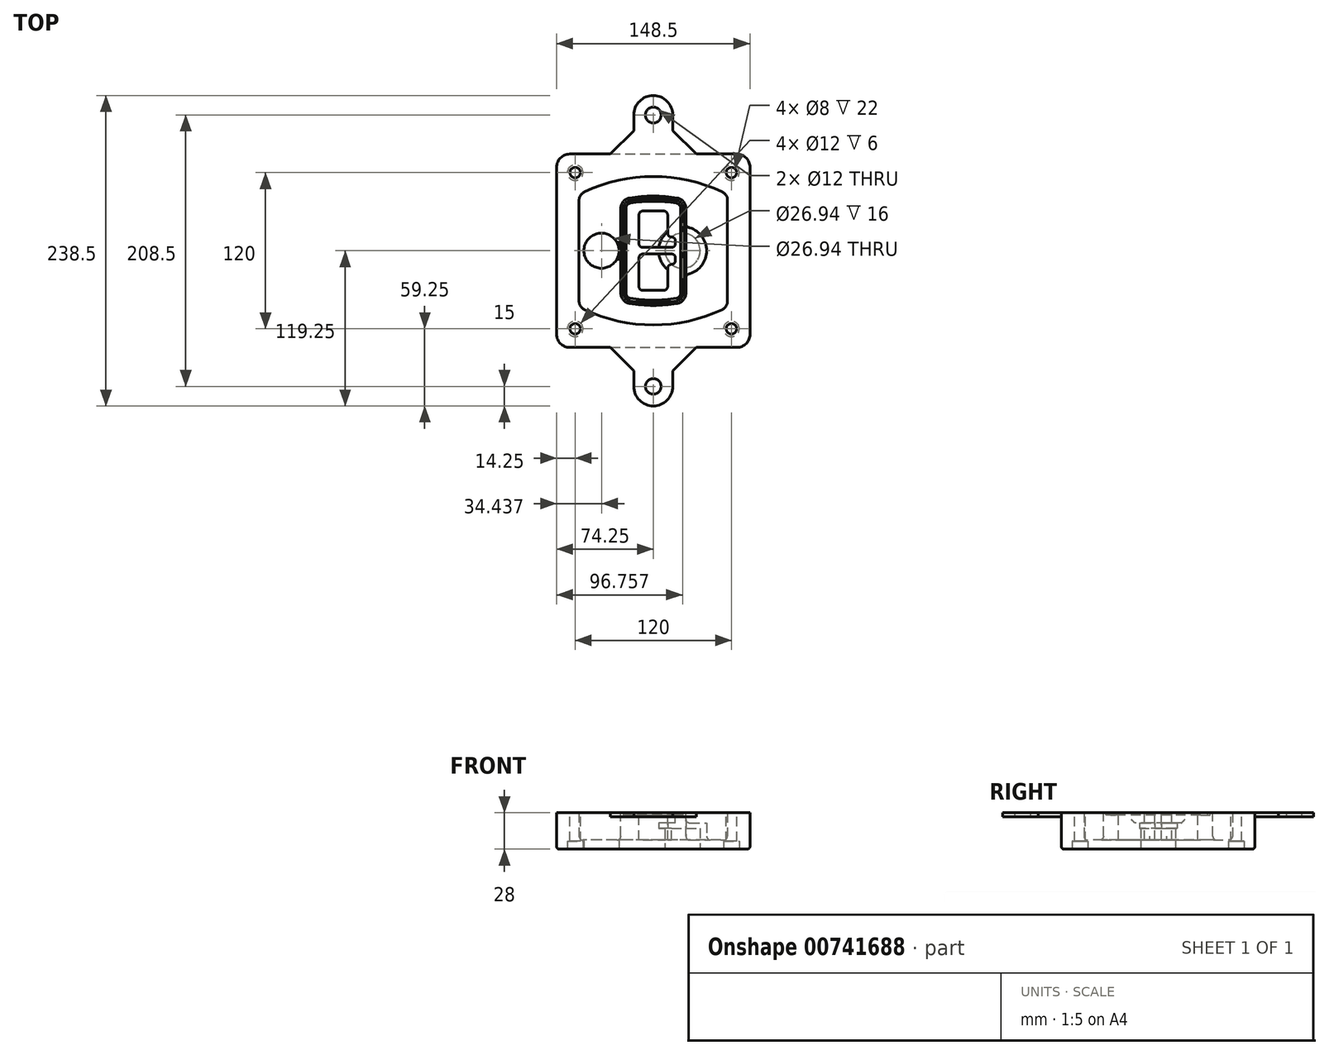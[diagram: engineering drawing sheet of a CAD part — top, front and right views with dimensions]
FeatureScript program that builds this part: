
annotation { "Feature Type Name" : "Feature", "Feature Type Description" : "" }
export const myFeature = defineFeature(function(context is Context, id is Id, definition is map)
    precondition{}
    {
        {
            var Q0;
            Q0=qCreatedBy(makeId("Top.planeOp"),FACE);
            var sketch = newSketch(context, id + "F0", { "sketchPlane" : qUnion([Q0])});
            skPoint(sketch, "E0.rect.middle", {"position": v(0, 0) * mm});
            skLineSegment(sketch, "E1.bottom", {"start": v(-64.25, -74.25) * mm, "end": v(64.25, -74.25) * mm});
            skLineSegment(sketch, "E1.top", {"start": v(-64.25, 74.25) * mm, "end": v(64.25, 74.25) * mm});
            skLineSegment(sketch, "E1.left", {"start": v(-74.25, -64.25) * mm, "end": v(-74.25, 64.25) * mm});
            skLineSegment(sketch, "E1.right", {"start": v(74.25, -64.25) * mm, "end": v(74.25, 64.25) * mm});
            skLineSegment(sketch, "E2", {"start": v(-74.25, 74.25) * mm, "end": v(74.25, -74.25) * mm, "construction": true});
            skLineSegment(sketch, "E3", {"start": v(74.25, 74.25) * mm, "end": v(-74.25, -74.25) * mm, "construction": true});
            skCircle(sketch, "E4", {"center": v(-60, 60) * mm, "radius": 4 * mm});
            skCircle(sketch, "E5", {"center": v(60, 60) * mm, "radius": 4 * mm});
            skCircle(sketch, "E6", {"center": v(60, -60) * mm, "radius": 4 * mm});
            skCircle(sketch, "E7", {"center": v(-60, -60) * mm, "radius": 4 * mm});
            skLineSegment(sketch, "E8", {"start": v(-60, 60) * mm, "end": v(60, 60) * mm, "construction": true});
            skLineSegment(sketch, "E9", {"start": v(60, 60) * mm, "end": v(60, -60) * mm, "construction": true});
            skLineSegment(sketch, "E10", {"start": v(60, -60) * mm, "end": v(-60, -60) * mm, "construction": true});
            skLineSegment(sketch, "E11", {"start": v(-60, -60) * mm, "end": v(-60, 60) * mm, "construction": true});
            skLineSegment(sketch, "E12", {"start": v(-60, 38.83) * mm, "end": v(-60, -38.83) * mm});
            skLineSegment(sketch, "E13", {"start": v(60, 38.83) * mm, "end": v(60, -38.83) * mm});
            skArc(sketch, "E14", {"start": v(54.26, 47.88) * mm, "mid": v(0, 60) * mm, "end": v(-54.26, 47.88) * mm});
            skArc(sketch, "E15", {"start": v(-54.26, -47.88) * mm, "mid": v(0, -60) * mm, "end": v(54.26, -47.88) * mm});
            skLineSegment(sketch, "E16", {"start": v(-60, 0) * mm, "end": v(60, 0) * mm, "construction": true});
            skPoint(sketch, "E17.visualSharp", {"position": v(-60, -45) * mm});
            skArc(sketch, "E17.filletArc", {"start": v(-60, -38.83) * mm, "mid": v(-58.44, -44.2) * mm, "end": v(-54.26, -47.88) * mm});
            skPoint(sketch, "E18.visualSharp", {"position": v(-60, 45) * mm});
            skArc(sketch, "E18.filletArc", {"start": v(-54.26, 47.88) * mm, "mid": v(-58.44, 44.2) * mm, "end": v(-60, 38.83) * mm});
            skPoint(sketch, "E19.visualSharp", {"position": v(60, 45) * mm});
            skArc(sketch, "E19.filletArc", {"start": v(60, 38.83) * mm, "mid": v(58.44, 44.2) * mm, "end": v(54.26, 47.88) * mm});
            skPoint(sketch, "E20.visualSharp", {"position": v(60, -45) * mm});
            skArc(sketch, "E20.filletArc", {"start": v(54.26, -47.88) * mm, "mid": v(58.44, -44.2) * mm, "end": v(60, -38.83) * mm});
            skPoint(sketch, "E21.visualSharp", {"position": v(-74.25, 74.25) * mm});
            skArc(sketch, "E21.filletArc", {"start": v(-64.25, 74.25) * mm, "mid": v(-71.32, 71.32) * mm, "end": v(-74.25, 64.25) * mm});
            skPoint(sketch, "E22.visualSharp", {"position": v(74.25, 74.25) * mm});
            skArc(sketch, "E22.filletArc", {"start": v(74.25, 64.25) * mm, "mid": v(71.32, 71.32) * mm, "end": v(64.25, 74.25) * mm});
            skPoint(sketch, "E23.visualSharp", {"position": v(74.25, -74.25) * mm});
            skArc(sketch, "E23.filletArc", {"start": v(64.25, -74.25) * mm, "mid": v(71.32, -71.32) * mm, "end": v(74.25, -64.25) * mm});
            skPoint(sketch, "E24.visualSharp", {"position": v(-74.25, -74.25) * mm});
            skArc(sketch, "E24.filletArc", {"start": v(-74.25, -64.25) * mm, "mid": v(-71.32, -71.32) * mm, "end": v(-64.25, -74.25) * mm});
            skArc(sketch, "E25.0", {"start": v(57, 38.83) * mm, "mid": v(55.9, 42.58) * mm, "end": v(52.98, 45.17) * mm});
            skLineSegment(sketch, "E25.1", {"start": v(57, 38.83) * mm, "end": v(57, -38.83) * mm});
            skArc(sketch, "E25.2", {"start": v(52.98, -45.17) * mm, "mid": v(55.9, -42.58) * mm, "end": v(57, -38.83) * mm});
            skArc(sketch, "E25.3", {"start": v(-52.98, -45.17) * mm, "mid": v(0, -57) * mm, "end": v(52.98, -45.17) * mm});
            skArc(sketch, "E25.4", {"start": v(-57, -38.83) * mm, "mid": v(-55.9, -42.58) * mm, "end": v(-52.98, -45.17) * mm});
            skArc(sketch, "E25.5", {"start": v(52.98, 45.17) * mm, "mid": v(0, 57) * mm, "end": v(-52.98, 45.17) * mm});
            skLineSegment(sketch, "E25.6", {"start": v(-57, 38.83) * mm, "end": v(-57, -38.83) * mm});
            skArc(sketch, "E25.7", {"start": v(-52.98, 45.17) * mm, "mid": v(-55.9, 42.58) * mm, "end": v(-57, 38.83) * mm});
            skArc(sketch, "E26.0", {"start": v(-55.96, 51.5) * mm, "mid": v(-61.82, 46.33) * mm, "end": v(-64, 38.83) * mm});
            skArc(sketch, "E26.1", {"start": v(55.96, 51.5) * mm, "mid": v(0, 64) * mm, "end": v(-55.96, 51.5) * mm});
            skArc(sketch, "E26.2", {"start": v(64, 38.83) * mm, "mid": v(61.82, 46.33) * mm, "end": v(55.96, 51.5) * mm});
            skLineSegment(sketch, "E26.3", {"start": v(64, 38.83) * mm, "end": v(64, -38.83) * mm});
            skArc(sketch, "E26.4", {"start": v(55.96, -51.5) * mm, "mid": v(61.82, -46.33) * mm, "end": v(64, -38.83) * mm});
            skLineSegment(sketch, "E26.5", {"start": v(-64, 38.83) * mm, "end": v(-64, -38.83) * mm});
            skArc(sketch, "E26.6", {"start": v(-55.96, -51.5) * mm, "mid": v(0, -64) * mm, "end": v(55.96, -51.5) * mm});
            skArc(sketch, "E26.7", {"start": v(-64, -38.83) * mm, "mid": v(-61.82, -46.33) * mm, "end": v(-55.96, -51.5) * mm});
            skSolve(sketch);
        }
        {
            var Q0;
            Q0=makeQuery(id+"F0.imprint","IMPRINT",FACE,{"disambiguationData":[TD([[makeQuery(id+"F0.imprint","IMPRINT",EDGE,{"derivedFrom":sQuery(id+"F0.wireOp",EDGE,"E1.bottom")}),1.0]])]});
            var Q1;
            Q1=makeQuery(id+"F0.imprint","IMPRINT",FACE,{"disambiguationData":[TD([[makeQuery(id+"F0.imprint","IMPRINT",EDGE,{"derivedFrom":sQuery(id+"F0.wireOp",EDGE,"E12")}),1.0]])]});
            var Q2;
            Q2=makeQuery(id+"F0.imprint","IMPRINT",FACE,{"disambiguationData":[TD([[makeQuery(id+"F0.imprint","IMPRINT",EDGE,{"derivedFrom":sQuery(id+"F0.wireOp",EDGE,"E25.0")}),1.0]])]});
            var Q3;
            Q3=makeQuery(id+"F0.imprint","IMPRINT",FACE,{"disambiguationData":[TD([[makeQuery(id+"F0.imprint","IMPRINT",EDGE,{"derivedFrom":sQuery(id+"F0.wireOp",EDGE,"E12")}),-1.0]])]});
            extrude(context, id + "F1", {"entities" : qUnion([Q0, Q1, Q2, Q3]), "oppositeDirection" : true, "depth" : 25 * mm});
        }
        {
            var Q0;
            Q0=makeQuery(id+"F0.imprint","IMPRINT",FACE,{"disambiguationData":[TD([[makeQuery(id+"F0.imprint","IMPRINT",EDGE,{"derivedFrom":sQuery(id+"F0.wireOp",EDGE,"E12")}),1.0]])]});
            extrude(context, id + "F2", {"entities" : qUnion([Q0]), "operationType" : NewBodyOperationType.ADD, "depth" : 3 * mm});
        }
        {
            var Q0;
            Q0=makeQuery(id+"F0.imprint","IMPRINT",FACE,{"disambiguationData":[TD([[makeQuery(id+"F0.imprint","IMPRINT",EDGE,{"derivedFrom":sQuery(id+"F0.wireOp",EDGE,"E25.0")}),1.0]])]});
            extrude(context, id + "F3", {"entities" : qUnion([Q0]), "operationType" : NewBodyOperationType.REMOVE, "oppositeDirection" : true, "depth" : 18 * mm});
        }
        {
            var Q0;
            Q0=makeQuery(id+"F2.opExtrude","CAP_FACE",FACE,{"disambiguationData":[OSD([sQuery(id+"F0.wireOp",EDGE,"E12"),sQuery(id+"F0.wireOp",EDGE,"E13"),sQuery(id+"F0.wireOp",EDGE,"E14"),sQuery(id+"F0.wireOp",EDGE,"E15"),sQuery(id+"F0.wireOp",EDGE,"E17.filletArc"),sQuery(id+"F0.wireOp",EDGE,"E18.filletArc"),sQuery(id+"F0.wireOp",EDGE,"E19.filletArc"),sQuery(id+"F0.wireOp",EDGE,"E20.filletArc"),sQuery(id+"F0.wireOp",EDGE,"E25.0"),sQuery(id+"F0.wireOp",EDGE,"E25.1"),sQuery(id+"F0.wireOp",EDGE,"E25.2"),sQuery(id+"F0.wireOp",EDGE,"E25.3"),sQuery(id+"F0.wireOp",EDGE,"E25.4"),sQuery(id+"F0.wireOp",EDGE,"E25.5"),sQuery(id+"F0.wireOp",EDGE,"E25.6"),sQuery(id+"F0.wireOp",EDGE,"E25.7")])],"isStart":false});
            var sketch = newSketch(context, id + "F4", { "sketchPlane" : qUnion([Q0])});
            skArc(sketch, "E27.0", {"start": v(-18.34, -40.45) * mm, "mid": v(0, -42) * mm, "end": v(18.34, -40.45) * mm});
            skArc(sketch, "E28.0", {"start": v(18.34, 40.45) * mm, "mid": v(0, 42) * mm, "end": v(-18.34, 40.45) * mm});
            skLineSegment(sketch, "E29", {"start": v(-25, 32.57) * mm, "end": v(-25, -32.57) * mm});
            skLineSegment(sketch, "E30", {"start": v(25, 32.57) * mm, "end": v(25, -32.57) * mm});
            skLineSegment(sketch, "E31", {"start": v(-25, 39.1) * mm, "end": v(25, 39.1) * mm, "construction": true});
            skLineSegment(sketch, "E32", {"start": v(-25, -39.1) * mm, "end": v(25, -39.1) * mm, "construction": true});
            skPoint(sketch, "E33.visualSharp", {"position": v(-25, 39.1) * mm});
            skArc(sketch, "E33.filletArc", {"start": v(-18.34, 40.45) * mm, "mid": v(-23.11, 37.73) * mm, "end": v(-25, 32.57) * mm});
            skPoint(sketch, "E34.visualSharp", {"position": v(25, 39.1) * mm});
            skArc(sketch, "E34.filletArc", {"start": v(25, 32.57) * mm, "mid": v(23.11, 37.73) * mm, "end": v(18.34, 40.45) * mm});
            skPoint(sketch, "E35.visualSharp", {"position": v(25, -39.1) * mm});
            skArc(sketch, "E35.filletArc", {"start": v(18.34, -40.45) * mm, "mid": v(23.11, -37.73) * mm, "end": v(25, -32.57) * mm});
            skPoint(sketch, "E36.visualSharp", {"position": v(-25, -39.1) * mm});
            skArc(sketch, "E36.filletArc", {"start": v(-25, -32.57) * mm, "mid": v(-23.11, -37.73) * mm, "end": v(-18.34, -40.45) * mm});
            skArc(sketch, "E37.0", {"start": v(52.98, 45.17) * mm, "mid": v(0, 57) * mm, "end": v(-52.98, 45.17) * mm});
            skArc(sketch, "E37.1", {"start": v(-52.98, 45.17) * mm, "mid": v(-55.9, 42.58) * mm, "end": v(-57, 38.83) * mm});
            skLineSegment(sketch, "E37.2", {"start": v(-57, 38.83) * mm, "end": v(-57, -38.83) * mm});
            skArc(sketch, "E37.3", {"start": v(-57, -38.83) * mm, "mid": v(-55.9, -42.58) * mm, "end": v(-52.98, -45.17) * mm});
            skArc(sketch, "E37.4", {"start": v(-52.98, -45.17) * mm, "mid": v(0, -57) * mm, "end": v(52.98, -45.17) * mm});
            skArc(sketch, "E37.5", {"start": v(52.98, -45.17) * mm, "mid": v(55.9, -42.58) * mm, "end": v(57, -38.83) * mm});
            skLineSegment(sketch, "E37.6", {"start": v(57, 38.83) * mm, "end": v(57, -38.83) * mm});
            skArc(sketch, "E37.7", {"start": v(57, 38.83) * mm, "mid": v(55.9, 42.58) * mm, "end": v(52.98, 45.17) * mm});
            skLineSegment(sketch, "E38.0", {"start": v(23, 32.57) * mm, "end": v(23, -32.57) * mm});
            skArc(sketch, "E38.1", {"start": v(18, -38.48) * mm, "mid": v(21.58, -36.44) * mm, "end": v(23, -32.57) * mm});
            skArc(sketch, "E38.2", {"start": v(-18, -38.48) * mm, "mid": v(0, -40) * mm, "end": v(18, -38.48) * mm});
            skArc(sketch, "E38.3", {"start": v(-23, -32.57) * mm, "mid": v(-21.58, -36.44) * mm, "end": v(-18, -38.48) * mm});
            skLineSegment(sketch, "E38.4", {"start": v(-23, 32.57) * mm, "end": v(-23, -32.57) * mm});
            skArc(sketch, "E38.5", {"start": v(23, 32.57) * mm, "mid": v(21.58, 36.44) * mm, "end": v(18, 38.48) * mm});
            skArc(sketch, "E38.6", {"start": v(-18, 38.48) * mm, "mid": v(-21.58, 36.44) * mm, "end": v(-23, 32.57) * mm});
            skArc(sketch, "E38.7", {"start": v(18, 38.48) * mm, "mid": v(0, 40) * mm, "end": v(-18, 38.48) * mm});
            skArc(sketch, "E39.0", {"start": v(21, 32.57) * mm, "mid": v(20.06, 35.15) * mm, "end": v(17.67, 36.5) * mm});
            skLineSegment(sketch, "E39.1", {"start": v(21, 32.57) * mm, "end": v(21, -32.57) * mm});
            skArc(sketch, "E39.2", {"start": v(17.67, -36.5) * mm, "mid": v(20.06, -35.15) * mm, "end": v(21, -32.57) * mm});
            skArc(sketch, "E39.3", {"start": v(-17.67, -36.5) * mm, "mid": v(0, -38) * mm, "end": v(17.67, -36.5) * mm});
            skArc(sketch, "E39.4", {"start": v(-21, -32.57) * mm, "mid": v(-20.06, -35.15) * mm, "end": v(-17.67, -36.5) * mm});
            skArc(sketch, "E39.5", {"start": v(17.67, 36.5) * mm, "mid": v(0, 38) * mm, "end": v(-17.67, 36.5) * mm});
            skLineSegment(sketch, "E39.6", {"start": v(-21, 32.57) * mm, "end": v(-21, -32.57) * mm});
            skArc(sketch, "E39.7", {"start": v(-17.67, 36.5) * mm, "mid": v(-20.06, 35.15) * mm, "end": v(-21, 32.57) * mm});
            skLineSegment(sketch, "E40", {"start": v(-25, 0) * mm, "end": v(25, 0) * mm, "construction": true});
            skLineSegment(sketch, "E41", {"start": v(-11, 5.5) * mm, "end": v(-11, 27.5) * mm});
            skLineSegment(sketch, "E42", {"start": v(-8, 30.5) * mm, "end": v(8, 30.5) * mm});
            skLineSegment(sketch, "E43", {"start": v(11, 27.5) * mm, "end": v(11, 13.5) * mm});
            skLineSegment(sketch, "E44", {"start": v(14, 10.5) * mm, "end": v(14, 10.5) * mm});
            skLineSegment(sketch, "E45", {"start": v(17, 7.5) * mm, "end": v(17, 5.5) * mm});
            skLineSegment(sketch, "E46", {"start": v(14, 2.5) * mm, "end": v(-8, 2.5) * mm});
            skPoint(sketch, "E47.visualSharp", {"position": v(-11, 30.5) * mm});
            skArc(sketch, "E47.filletArc", {"start": v(-8, 30.5) * mm, "mid": v(-10.12, 29.62) * mm, "end": v(-11, 27.5) * mm});
            skPoint(sketch, "E48.visualSharp", {"position": v(11, 30.5) * mm});
            skArc(sketch, "E48.filletArc", {"start": v(11, 27.5) * mm, "mid": v(10.12, 29.62) * mm, "end": v(8, 30.5) * mm});
            skPoint(sketch, "E49.visualSharp", {"position": v(11, 10.5) * mm});
            skArc(sketch, "E49.filletArc", {"start": v(11, 13.5) * mm, "mid": v(11.88, 11.38) * mm, "end": v(14, 10.5) * mm});
            skPoint(sketch, "E50.visualSharp", {"position": v(17, 10.5) * mm});
            skArc(sketch, "E50.filletArc", {"start": v(17, 7.5) * mm, "mid": v(16.12, 9.62) * mm, "end": v(14, 10.5) * mm});
            skPoint(sketch, "E51.visualSharp", {"position": v(17, 2.5) * mm});
            skArc(sketch, "E51.filletArc", {"start": v(14, 2.5) * mm, "mid": v(16.12, 3.38) * mm, "end": v(17, 5.5) * mm});
            skPoint(sketch, "E52.visualSharp", {"position": v(-11, 2.5) * mm});
            skArc(sketch, "E52.filletArc", {"start": v(-11, 5.5) * mm, "mid": v(-10.12, 3.38) * mm, "end": v(-8, 2.5) * mm});
            skLineSegment(sketch, "E53.0.MirrorCS", {"start": v(14, -2.5) * mm, "end": v(-8, -2.5) * mm});
            skArc(sketch, "E54.0.MirrorCS", {"start": v(-11, -5.5) * mm, "mid": v(-10.12, -3.38) * mm, "end": v(-8, -2.5) * mm});
            skLineSegment(sketch, "E55.0.MirrorCS", {"start": v(-11, -5.5) * mm, "end": v(-11, -27.5) * mm});
            skArc(sketch, "E56.0.MirrorCS", {"start": v(-8, -30.5) * mm, "mid": v(-10.12, -29.62) * mm, "end": v(-11, -27.5) * mm});
            skLineSegment(sketch, "E57.0.MirrorCS", {"start": v(-8, -30.5) * mm, "end": v(8, -30.5) * mm});
            skArc(sketch, "E58.0.MirrorCS", {"start": v(11, -27.5) * mm, "mid": v(10.12, -29.62) * mm, "end": v(8, -30.5) * mm});
            skLineSegment(sketch, "E59.0.MirrorCS", {"start": v(11, -27.5) * mm, "end": v(11, -13.5) * mm});
            skArc(sketch, "E60.0.MirrorCS", {"start": v(11, -13.5) * mm, "mid": v(11.88, -11.38) * mm, "end": v(14, -10.5) * mm});
            skArc(sketch, "E61.0.MirrorCS", {"start": v(17, -7.5) * mm, "mid": v(16.12, -9.62) * mm, "end": v(14, -10.5) * mm});
            skLineSegment(sketch, "E62.0.MirrorCS", {"start": v(17, -7.5) * mm, "end": v(17, -5.5) * mm});
            skArc(sketch, "E63.0.MirrorCS", {"start": v(14, -2.5) * mm, "mid": v(16.12, -3.38) * mm, "end": v(17, -5.5) * mm});
            skSolve(sketch);
        }
        {
            var Q0;
            Q0=makeQuery(id+"F4.imprint","IMPRINT",FACE,{"disambiguationData":[TD([[makeQuery(id+"F4.imprint","IMPRINT",EDGE,{"derivedFrom":sQuery(id+"F4.wireOp",EDGE,"E27.0")}),1.0]])]});
            var Q1;
            Q1=makeQuery(id+"F4.imprint","IMPRINT",FACE,{"disambiguationData":[TD([[makeQuery(id+"F4.imprint","IMPRINT",EDGE,{"derivedFrom":sQuery(id+"F4.wireOp",EDGE,"E38.0")}),-1.0]])]});
            var Q2;
            Q2=makeQuery(id+"F4.imprint","IMPRINT",FACE,{"disambiguationData":[TD([[makeQuery(id+"F4.imprint","IMPRINT",EDGE,{"derivedFrom":sQuery(id+"F4.wireOp",EDGE,"E39.0")}),1.0]])]});
            extrude(context, id + "F5", {"entities" : qUnion([Q0, Q1, Q2]), "operationType" : NewBodyOperationType.ADD, "endBound" : BoundingType.UP_TO_NEXT, "oppositeDirection" : true, "depth" : 25 * mm});
        }
        {
            var Q0;
            Q0=makeQuery(id+"F4.imprint","IMPRINT",FACE,{"disambiguationData":[TD([[makeQuery(id+"F4.imprint","IMPRINT",EDGE,{"derivedFrom":sQuery(id+"F4.wireOp",EDGE,"E38.0")}),-1.0]])]});
            extrude(context, id + "F6", {"entities" : qUnion([Q0]), "operationType" : NewBodyOperationType.REMOVE, "oppositeDirection" : true, "depth" : 2 * mm});
        }
        {
            var Q0;
            Q0=makeQuery(id+"F1.opExtrude","CAP_FACE",FACE,{"disambiguationData":[OSD([sQuery(id+"F0.wireOp",EDGE,"E1.bottom"),sQuery(id+"F0.wireOp",EDGE,"E1.top"),sQuery(id+"F0.wireOp",EDGE,"E1.left"),sQuery(id+"F0.wireOp",EDGE,"E1.right"),sQuery(id+"F0.wireOp",EDGE,"E4"),sQuery(id+"F0.wireOp",EDGE,"E5"),sQuery(id+"F0.wireOp",EDGE,"E6"),sQuery(id+"F0.wireOp",EDGE,"E7"),sQuery(id+"F0.wireOp",EDGE,"E21.filletArc"),sQuery(id+"F0.wireOp",EDGE,"E22.filletArc"),sQuery(id+"F0.wireOp",EDGE,"E23.filletArc"),sQuery(id+"F0.wireOp",EDGE,"E24.filletArc")])],"isStart":false});
            var sketch = newSketch(context, id + "F7", { "sketchPlane" : qUnion([Q0])});
            skCircle(sketch, "E64", {"center": v(22.5, 0) * mm, "radius": 13.47 * mm});
            skCircle(sketch, "E65", {"center": v(-39.81, 0) * mm, "radius": 13.47 * mm});
            skLineSegment(sketch, "E66", {"start": v(74.25, 0) * mm, "end": v(-74.25, 0) * mm});
            skCircle(sketch, "E67", {"center": v(22.5, 0) * mm, "radius": 18.47 * mm});
            skCircle(sketch, "E68", {"center": v(60, -60) * mm, "radius": 6 * mm});
            skCircle(sketch, "E69", {"center": v(-60, -60) * mm, "radius": 6 * mm});
            skCircle(sketch, "E70", {"center": v(-60, 60) * mm, "radius": 6 * mm});
            skCircle(sketch, "E71", {"center": v(60, 60) * mm, "radius": 6 * mm});
            skSolve(sketch);
        }
        {
            var Q0;
            {var subQ1=sQuery(id+"F7.wireOp",EDGE,"E66");var subQ4=sQuery(id+"F7.wireOp",EDGE,"E64");var subQ6=makeQuery(id+"F7.imprint","INTERSECT",VERTEX,{"disambiguationData":[OD(0.0)],"derivedFrom":[subQ4,subQ1]});Q0=makeQuery(id+"F7.imprint","IMPRINT",FACE,{"disambiguationData":[TD([[makeQuery(id+"F7.imprint","IMPRINT",EDGE,{"disambiguationData":[TD([[subQ6,-1.0]])],"derivedFrom":subQ4}),-1.0]])]});}
            var Q1;
            {var subQ0=sQuery(id+"F7.wireOp",EDGE,"E66");var subQ1=sQuery(id+"F7.wireOp",EDGE,"E64");var subQ3=makeQuery(id+"F7.imprint","INTERSECT",VERTEX,{"disambiguationData":[OD(0.0)],"derivedFrom":[subQ1,subQ0]});Q1=makeQuery(id+"F7.imprint","IMPRINT",FACE,{"disambiguationData":[TD([[makeQuery(id+"F7.imprint","IMPRINT",EDGE,{"disambiguationData":[TD([[subQ3,-1.0]])],"derivedFrom":subQ1}),1.0]])]});}
            var Q2;
            {var subQ0=sQuery(id+"F7.wireOp",EDGE,"E66");var subQ1=sQuery(id+"F7.wireOp",EDGE,"E64");var subQ3=makeQuery(id+"F7.imprint","INTERSECT",VERTEX,{"disambiguationData":[OD(0.0)],"derivedFrom":[subQ1,subQ0]});Q2=makeQuery(id+"F7.imprint","IMPRINT",FACE,{"disambiguationData":[TD([[makeQuery(id+"F7.imprint","IMPRINT",EDGE,{"disambiguationData":[TD([[subQ3,1.0]])],"derivedFrom":subQ1}),1.0]])]});}
            var Q3;
            {var subQ1=sQuery(id+"F7.wireOp",EDGE,"E66");var subQ4=sQuery(id+"F7.wireOp",EDGE,"E64");var subQ6=makeQuery(id+"F7.imprint","INTERSECT",VERTEX,{"disambiguationData":[OD(0.0)],"derivedFrom":[subQ4,subQ1]});Q3=makeQuery(id+"F7.imprint","IMPRINT",FACE,{"disambiguationData":[TD([[makeQuery(id+"F7.imprint","IMPRINT",EDGE,{"disambiguationData":[TD([[subQ6,1.0]])],"derivedFrom":subQ4}),-1.0]])]});}
            extrude(context, id + "F8", {"entities" : qUnion([Q0, Q1, Q2, Q3]), "operationType" : NewBodyOperationType.ADD, "oppositeDirection" : true, "depth" : 20 * mm});
        }
        {
            var Q0;
            {var subQ0=sQuery(id+"F7.wireOp",EDGE,"E66");var subQ1=sQuery(id+"F7.wireOp",EDGE,"E64");var subQ3=makeQuery(id+"F7.imprint","INTERSECT",VERTEX,{"disambiguationData":[OD(0.0)],"derivedFrom":[subQ1,subQ0]});Q0=makeQuery(id+"F7.imprint","IMPRINT",FACE,{"disambiguationData":[TD([[makeQuery(id+"F7.imprint","IMPRINT",EDGE,{"disambiguationData":[TD([[subQ3,-1.0]])],"derivedFrom":subQ1}),1.0]])]});}
            var Q1;
            {var subQ0=sQuery(id+"F7.wireOp",EDGE,"E66");var subQ1=sQuery(id+"F7.wireOp",EDGE,"E64");var subQ3=makeQuery(id+"F7.imprint","INTERSECT",VERTEX,{"disambiguationData":[OD(0.0)],"derivedFrom":[subQ1,subQ0]});Q1=makeQuery(id+"F7.imprint","IMPRINT",FACE,{"disambiguationData":[TD([[makeQuery(id+"F7.imprint","IMPRINT",EDGE,{"disambiguationData":[TD([[subQ3,1.0]])],"derivedFrom":subQ1}),1.0]])]});}
            extrude(context, id + "F9", {"entities" : qUnion([Q0, Q1]), "operationType" : NewBodyOperationType.REMOVE, "oppositeDirection" : true, "depth" : 16 * mm});
        }
        {
            var Q0;
            {var subQ0=sQuery(id+"F7.wireOp",EDGE,"E66");var subQ1=sQuery(id+"F7.wireOp",EDGE,"E65");var subQ3=makeQuery(id+"F7.imprint","INTERSECT",VERTEX,{"disambiguationData":[OD(0.0)],"derivedFrom":[subQ1,subQ0]});Q0=makeQuery(id+"F7.imprint","IMPRINT",FACE,{"disambiguationData":[TD([[makeQuery(id+"F7.imprint","IMPRINT",EDGE,{"disambiguationData":[TD([[subQ3,-1.0]])],"derivedFrom":subQ1}),1.0]])]});}
            var Q1;
            {var subQ0=sQuery(id+"F7.wireOp",EDGE,"E66");var subQ1=sQuery(id+"F7.wireOp",EDGE,"E65");var subQ3=makeQuery(id+"F7.imprint","INTERSECT",VERTEX,{"disambiguationData":[OD(0.0)],"derivedFrom":[subQ1,subQ0]});Q1=makeQuery(id+"F7.imprint","IMPRINT",FACE,{"disambiguationData":[TD([[makeQuery(id+"F7.imprint","IMPRINT",EDGE,{"disambiguationData":[TD([[subQ3,1.0]])],"derivedFrom":subQ1}),1.0]])]});}
            extrude(context, id + "F10", {"entities" : qUnion([Q0, Q1]), "operationType" : NewBodyOperationType.REMOVE, "oppositeDirection" : true, "depth" : 25 * mm});
        }
        {
            var Q0;
            Q0=makeQuery(id+"F7.imprint","IMPRINT",FACE,{"disambiguationData":[TD([[makeQuery(id+"F7.imprint","IMPRINT",EDGE,{"derivedFrom":sQuery(id+"F7.wireOp",EDGE,"E68")}),1.0]])]});
            var Q1;
            Q1=makeQuery(id+"F7.imprint","IMPRINT",FACE,{"disambiguationData":[TD([[makeQuery(id+"F7.imprint","IMPRINT",EDGE,{"derivedFrom":makeQuery(id+"F1.opExtrude","CAP_EDGE",EDGE,{"disambiguationData":[OSD([sQuery(id+"F0.wireOp",EDGE,"E5")])],"isStart":false})}),-1.0]])]});
            var Q2;
            Q2=makeQuery(id+"F7.imprint","IMPRINT",FACE,{"disambiguationData":[TD([[makeQuery(id+"F7.imprint","IMPRINT",EDGE,{"derivedFrom":sQuery(id+"F7.wireOp",EDGE,"E69")}),1.0]])]});
            var Q3;
            Q3=makeQuery(id+"F7.imprint","IMPRINT",FACE,{"disambiguationData":[TD([[makeQuery(id+"F7.imprint","IMPRINT",EDGE,{"derivedFrom":makeQuery(id+"F1.opExtrude","CAP_EDGE",EDGE,{"disambiguationData":[OSD([sQuery(id+"F0.wireOp",EDGE,"E4")])],"isStart":false})}),-1.0]])]});
            var Q4;
            Q4=makeQuery(id+"F7.imprint","IMPRINT",FACE,{"disambiguationData":[TD([[makeQuery(id+"F7.imprint","IMPRINT",EDGE,{"derivedFrom":sQuery(id+"F7.wireOp",EDGE,"E70")}),1.0]])]});
            var Q5;
            Q5=makeQuery(id+"F7.imprint","IMPRINT",FACE,{"disambiguationData":[TD([[makeQuery(id+"F7.imprint","IMPRINT",EDGE,{"derivedFrom":makeQuery(id+"F1.opExtrude","CAP_EDGE",EDGE,{"disambiguationData":[OSD([sQuery(id+"F0.wireOp",EDGE,"E7")])],"isStart":false})}),-1.0]])]});
            var Q6;
            Q6=makeQuery(id+"F7.imprint","IMPRINT",FACE,{"disambiguationData":[TD([[makeQuery(id+"F7.imprint","IMPRINT",EDGE,{"derivedFrom":sQuery(id+"F7.wireOp",EDGE,"E71")}),1.0]])]});
            var Q7;
            Q7=makeQuery(id+"F7.imprint","IMPRINT",FACE,{"disambiguationData":[TD([[makeQuery(id+"F7.imprint","IMPRINT",EDGE,{"derivedFrom":makeQuery(id+"F1.opExtrude","CAP_EDGE",EDGE,{"disambiguationData":[OSD([sQuery(id+"F0.wireOp",EDGE,"E6")])],"isStart":false})}),-1.0]])]});
            extrude(context, id + "F11", {"entities" : qUnion([Q0, Q1, Q2, Q3, Q4, Q5, Q6, Q7]), "operationType" : NewBodyOperationType.REMOVE, "oppositeDirection" : true, "depth" : 6 * mm});
        }
        {
            var Q0;
            Q0=makeQuery(id+"F9.boolean.opBoolean","COPY",FACE,{"derivedFrom":makeQuery(id+"F9.opExtrude","CAP_FACE",FACE,{"disambiguationData":[OSD([sQuery(id+"F7.wireOp",EDGE,"E64")])],"isStart":false})});
            var sketch = newSketch(context, id + "F12", { "sketchPlane" : qUnion([Q0])});
            skArc(sketch, "E72.0", {"start": v(11, 14.45) * mm, "mid": v(6.45, 9.13) * mm, "end": v(4.2, 2.5) * mm});
            skArc(sketch, "E72.1", {"start": v(4.2, -2.5) * mm, "mid": v(6.45, -9.13) * mm, "end": v(11, -14.45) * mm});
            skLineSegment(sketch, "E73", {"start": v(4.2, -2.5) * mm, "end": v(14, -2.5) * mm});
            skLineSegment(sketch, "E74.0", {"start": v(14, 2.5) * mm, "end": v(4.2, 2.5) * mm});
            skArc(sketch, "E74.1", {"start": v(14, 2.5) * mm, "mid": v(16.12, 3.38) * mm, "end": v(17, 5.5) * mm});
            skLineSegment(sketch, "E74.2", {"start": v(17, 7.5) * mm, "end": v(17, 5.5) * mm});
            skArc(sketch, "E74.3", {"start": v(17, 7.5) * mm, "mid": v(16.12, 9.62) * mm, "end": v(14, 10.5) * mm});
            skArc(sketch, "E74.4", {"start": v(11, 13.5) * mm, "mid": v(11.88, 11.38) * mm, "end": v(14, 10.5) * mm});
            skLineSegment(sketch, "E74.5", {"start": v(11, 14.45) * mm, "end": v(11, 13.5) * mm});
            skLineSegment(sketch, "E74.7", {"start": v(14, -2.5) * mm, "end": v(4.2, -2.5) * mm});
            skArc(sketch, "E74.8", {"start": v(14, -2.5) * mm, "mid": v(16.12, -3.38) * mm, "end": v(17, -5.5) * mm});
            skLineSegment(sketch, "E74.9", {"start": v(17, -7.5) * mm, "end": v(17, -5.5) * mm});
            skArc(sketch, "E74.10", {"start": v(17, -7.5) * mm, "mid": v(16.12, -9.62) * mm, "end": v(14, -10.5) * mm});
            skArc(sketch, "E74.11", {"start": v(11, -13.5) * mm, "mid": v(11.88, -11.38) * mm, "end": v(14, -10.5) * mm});
            skLineSegment(sketch, "E74.12", {"start": v(11, -14.45) * mm, "end": v(11, -13.5) * mm});
            skPoint(sketch, "E75.orphan", {"position": v(11, -27.5) * mm});
            skPoint(sketch, "E76.orphan", {"position": v(-8, -2.5) * mm});
            skPoint(sketch, "E77.orphan", {"position": v(-8, 2.5) * mm});
            skPoint(sketch, "E78.orphan", {"position": v(11, 27.5) * mm});
            skSolve(sketch);
        }
        {
            var Q0;
            {var subQ7=sQuery(id+"F12.wireOp",EDGE,"E72.0");var subQ14=sQuery(id+"F12.wireOp",EDGE,"E72.1");var subQ16=sQuery(id+"F12.wireOp",EDGE,"E74.1");var subQ18=sQuery(id+"F12.wireOp",EDGE,"E74.8");Q0=qUnion([makeQuery(id+"F12.imprint","IMPRINT",FACE,{"disambiguationData":[TD([[makeQuery(id+"F12.imprint","IMPRINT",EDGE,{"derivedFrom":subQ7}),1.0]])]}),makeQuery(id+"F12.imprint","IMPRINT",FACE,{"disambiguationData":[TD([[makeQuery(id+"F12.imprint","IMPRINT",EDGE,{"derivedFrom":subQ14}),1.0]])]}),makeQuery(id+"F12.imprint","IMPRINT",FACE,{"disambiguationData":[TD([[makeQuery(id+"F12.imprint","IMPRINT",EDGE,{"derivedFrom":subQ16}),1.0]])]}),makeQuery(id+"F12.imprint","IMPRINT",FACE,{"disambiguationData":[TD([[makeQuery(id+"F12.imprint","IMPRINT",EDGE,{"derivedFrom":subQ18}),-1.0]])]})]);}
            var Q1;
            Q1=makeQuery(id+"F5.boolean.opBoolean","SPLIT",FACE,{"disambiguationData":[TD([makeQuery(id+"F5.opExtrude","SWEPT_FACE",FACE,{"disambiguationData":[OSD([sQuery(id+"F4.wireOp",EDGE,"E41")])]})])],"derivedFrom":makeQuery(id+"F3.boolean.opBoolean","COPY",FACE,{"derivedFrom":makeQuery(id+"F3.opExtrude","CAP_FACE",FACE,{"disambiguationData":[OSD([sQuery(id+"F0.wireOp",EDGE,"E25.0"),sQuery(id+"F0.wireOp",EDGE,"E25.1"),sQuery(id+"F0.wireOp",EDGE,"E25.2"),sQuery(id+"F0.wireOp",EDGE,"E25.3"),sQuery(id+"F0.wireOp",EDGE,"E25.4"),sQuery(id+"F0.wireOp",EDGE,"E25.5"),sQuery(id+"F0.wireOp",EDGE,"E25.6"),sQuery(id+"F0.wireOp",EDGE,"E25.7")])],"isStart":false})})});
            extrude(context, id + "F13", {"entities" : qUnion([Q0]), "operationType" : NewBodyOperationType.REMOVE, "endBound" : BoundingType.UP_TO_SURFACE, "endBoundEntityFace" : qUnion([Q1]), "depth" : 25 * mm});
        }
        {
            var Q0;
            Q0=makeQuery(id+"F3.boolean.opBoolean","COPY",EDGE,{"derivedFrom":makeQuery(id+"F3.opExtrude","CAP_EDGE",EDGE,{"disambiguationData":[OSD([sQuery(id+"F0.wireOp",EDGE,"E25.6")])],"isStart":false})});
            var Q1;
            Q1=makeQuery(id+"F8.boolean.opBoolean","INTERSECT",EDGE,{"derivedFrom":[makeQuery(id+"F5.opExtrude","SWEPT_FACE",FACE,{"disambiguationData":[OSD([sQuery(id+"F4.wireOp",EDGE,"E30")])]}),makeQuery(id+"F8.opExtrude","CAP_FACE",FACE,{"disambiguationData":[OSD([sQuery(id+"F7.wireOp",EDGE,"E67")])],"isStart":false})]});
            var Q2;
            Q2=makeQuery(id+"F8.boolean.opBoolean","INTERSECT",EDGE,{"disambiguationData":[OD(1.0)],"derivedFrom":[makeQuery(id+"F5.opExtrude","SWEPT_FACE",FACE,{"disambiguationData":[OSD([sQuery(id+"F4.wireOp",EDGE,"E30")])]}),makeQuery(id+"F8.opExtrude","SWEPT_FACE",FACE,{"disambiguationData":[OSD([sQuery(id+"F7.wireOp",EDGE,"E67")])]})]});
            var Q3;
            {var subQ0=sQuery(id+"F4.wireOp",EDGE,"E30");Q3=makeQuery(id+"F8.boolean.opBoolean","SPLIT",EDGE,{"disambiguationData":[TD([makeQuery(id+"F5.opExtrude","SWEPT_FACE",FACE,{"disambiguationData":[OSD([sQuery(id+"F4.wireOp",EDGE,"E35.filletArc")])]})])],"derivedFrom":makeQuery(id+"F5.opExtrude","CAP_EDGE",EDGE,{"disambiguationData":[OSD([subQ0])],"isStart":false})});}
            var Q4;
            {var subQ0=sQuery(id+"F0.wireOp",EDGE,"E25.7");var subQ1=sQuery(id+"F0.wireOp",EDGE,"E25.1");var subQ2=sQuery(id+"F0.wireOp",EDGE,"E25.6");var subQ3=sQuery(id+"F0.wireOp",EDGE,"E25.5");var subQ4=sQuery(id+"F0.wireOp",EDGE,"E25.4");var subQ5=sQuery(id+"F0.wireOp",EDGE,"E25.0");var subQ6=sQuery(id+"F0.wireOp",EDGE,"E25.2");var subQ7=sQuery(id+"F0.wireOp",EDGE,"E25.3");Q4=makeQuery(id+"F8.boolean.opBoolean","INTERSECT",EDGE,{"derivedFrom":[makeQuery(id+"F5.boolean.opBoolean","SPLIT",FACE,{"disambiguationData":[TD([makeQuery(id+"F2.opExtrude","SWEPT_FACE",FACE,{"disambiguationData":[OSD([subQ5])]})])],"derivedFrom":makeQuery(id+"F3.boolean.opBoolean","COPY",FACE,{"derivedFrom":makeQuery(id+"F3.opExtrude","CAP_FACE",FACE,{"disambiguationData":[OSD([subQ5,subQ1,subQ6,subQ7,subQ4,subQ3,subQ2,subQ0])],"isStart":false})})}),makeQuery(id+"F8.opExtrude","SWEPT_FACE",FACE,{"disambiguationData":[OSD([sQuery(id+"F7.wireOp",EDGE,"E67")])]})]});}
            var Q5;
            Q5=makeQuery(id+"F8.boolean.opBoolean","INTERSECT",EDGE,{"disambiguationData":[OD(0.0)],"derivedFrom":[makeQuery(id+"F5.opExtrude","SWEPT_FACE",FACE,{"disambiguationData":[OSD([sQuery(id+"F4.wireOp",EDGE,"E30")])]}),makeQuery(id+"F8.opExtrude","SWEPT_FACE",FACE,{"disambiguationData":[OSD([sQuery(id+"F7.wireOp",EDGE,"E67")])]})]});
            fillet(context, id + "F14", {"entities" : qUnion([Q0, Q1, Q2, Q3, Q4, Q5]), "radius" : 3 * mm, "tangentPropagation" : true, "allowEdgeOverflow" : false});
        }
        {
            var Q0;
            Q0=makeQuery(id+"F1.opExtrude","CAP_EDGE",EDGE,{"disambiguationData":[OSD([sQuery(id+"F0.wireOp",EDGE,"E1.bottom")])],"isStart":false});
            fillet(context, id + "F15", {"entities" : qUnion([Q0]), "radius" : 2 * mm, "tangentPropagation" : true, "allowEdgeOverflow" : false});
        }
        {
            var Q0;
            {var subQ0=sQuery(id+"F0.wireOp",EDGE,"E21.filletArc");var subQ1=sQuery(id+"F0.wireOp",EDGE,"E7");var subQ2=sQuery(id+"F0.wireOp",EDGE,"E6");var subQ3=sQuery(id+"F0.wireOp",EDGE,"E5");var subQ4=sQuery(id+"F0.wireOp",EDGE,"E4");var subQ5=sQuery(id+"F0.wireOp",EDGE,"E22.filletArc");var subQ6=sQuery(id+"F0.wireOp",EDGE,"E1.bottom");var subQ7=sQuery(id+"F0.wireOp",EDGE,"E1.right");var subQ8=sQuery(id+"F0.wireOp",EDGE,"E1.top");var subQ9=sQuery(id+"F0.wireOp",EDGE,"E1.left");var subQ10=sQuery(id+"F0.wireOp",EDGE,"E23.filletArc");var subQ11=sQuery(id+"F0.wireOp",EDGE,"E24.filletArc");Q0=makeQuery(id+"F2.boolean.opBoolean","SPLIT",FACE,{"disambiguationData":[TD([makeQuery(id+"F1.opExtrude","SWEPT_FACE",FACE,{"disambiguationData":[OSD([subQ6])]})])],"derivedFrom":makeQuery(id+"F1.opExtrude","CAP_FACE",FACE,{"disambiguationData":[OSD([subQ6,subQ8,subQ9,subQ7,subQ4,subQ3,subQ2,subQ1,subQ0,subQ5,subQ10,subQ11])],"isStart":true})});}
            var sketch = newSketch(context, id + "F16", { "sketchPlane" : qUnion([Q0])});
            skLineSegment(sketch, "E79", {"start": v(0, 74.25) * mm, "end": v(0, 104.25) * mm, "construction": true});
            skCircle(sketch, "E80", {"center": v(0, 104.25) * mm, "radius": 6 * mm});
            skLineSegment(sketch, "E81", {"start": v(-33, 74.25) * mm, "end": v(-15, 92.25) * mm});
            skLineSegment(sketch, "E82", {"start": v(-15, 92.25) * mm, "end": v(-15, 104.25) * mm});
            skLineSegment(sketch, "E83.MirrorCS", {"start": v(15, 92.25) * mm, "end": v(15, 104.25) * mm});
            skLineSegment(sketch, "E84.MirrorCS", {"start": v(33, 74.25) * mm, "end": v(15, 92.25) * mm});
            skArc(sketch, "E85", {"start": v(15, 104.25) * mm, "mid": v(0, 119.25) * mm, "end": v(-15, 104.25) * mm});
            skLineSegment(sketch, "E86", {"start": v(-74.25, 0) * mm, "end": v(74.25, 0) * mm, "construction": true});
            skLineSegment(sketch, "E87.MirrorCS", {"start": v(15, -92.25) * mm, "end": v(15, -104.25) * mm});
            skLineSegment(sketch, "E88.MirrorCS", {"start": v(33, -74.25) * mm, "end": v(15, -92.25) * mm});
            skCircle(sketch, "E89.MirrorC", {"center": v(0, -104.25) * mm, "radius": 6 * mm});
            skLineSegment(sketch, "E90.MirrorCS", {"start": v(0, -74.25) * mm, "end": v(0, -104.25) * mm, "construction": true});
            skLineSegment(sketch, "E91.MirrorCS", {"start": v(-15, -92.25) * mm, "end": v(-15, -104.25) * mm});
            skArc(sketch, "E92.MirrorCS", {"start": v(15, -104.25) * mm, "mid": v(0, -119.25) * mm, "end": v(-15, -104.25) * mm});
            skLineSegment(sketch, "E93.MirrorCS", {"start": v(-33, -74.25) * mm, "end": v(-15, -92.25) * mm});
            skSolve(sketch);
        }
        {
            var Q0;
            Q0=makeQuery(id+"F16.imprint","IMPRINT",FACE,{"disambiguationData":[TD([[makeQuery(id+"F16.imprint","IMPRINT",EDGE,{"derivedFrom":sQuery(id+"F16.wireOp",EDGE,"E80")}),-1.0]])]});
            var Q1;
            Q1=makeQuery(id+"F16.imprint","IMPRINT",FACE,{"disambiguationData":[TD([[makeQuery(id+"F16.imprint","IMPRINT",EDGE,{"derivedFrom":sQuery(id+"F16.wireOp",EDGE,"E87.MirrorCS")}),-1.0]])]});
            var Q2;
            Q2=makeQuery(id+"F16.imprint","IMPRINT",FACE,{"disambiguationData":[TD([[makeQuery(id+"F16.imprint","IMPRINT",EDGE,{"derivedFrom":makeQuery(id+"F1.opExtrude","CAP_EDGE",EDGE,{"disambiguationData":[OSD([sQuery(id+"F0.wireOp",EDGE,"E1.left")])],"isStart":true})}),-1.0]])]});
            var Q3;
            Q3=makeQuery(id+"F2.opExtrude","CAP_FACE",FACE,{"disambiguationData":[OSD([sQuery(id+"F0.wireOp",EDGE,"E12"),sQuery(id+"F0.wireOp",EDGE,"E13"),sQuery(id+"F0.wireOp",EDGE,"E14"),sQuery(id+"F0.wireOp",EDGE,"E15"),sQuery(id+"F0.wireOp",EDGE,"E17.filletArc"),sQuery(id+"F0.wireOp",EDGE,"E18.filletArc"),sQuery(id+"F0.wireOp",EDGE,"E19.filletArc"),sQuery(id+"F0.wireOp",EDGE,"E20.filletArc"),sQuery(id+"F0.wireOp",EDGE,"E25.0"),sQuery(id+"F0.wireOp",EDGE,"E25.1"),sQuery(id+"F0.wireOp",EDGE,"E25.2"),sQuery(id+"F0.wireOp",EDGE,"E25.3"),sQuery(id+"F0.wireOp",EDGE,"E25.4"),sQuery(id+"F0.wireOp",EDGE,"E25.5"),sQuery(id+"F0.wireOp",EDGE,"E25.6"),sQuery(id+"F0.wireOp",EDGE,"E25.7")])],"isStart":false});
            extrude(context, id + "F17", {"entities" : qUnion([Q0, Q1, Q2]), "operationType" : NewBodyOperationType.ADD, "endBound" : BoundingType.UP_TO_SURFACE, "depth" : 25 * mm, "endBoundEntityFace" : qUnion([Q3]), "offsetDistance" : 25 * mm});
        }
    });
